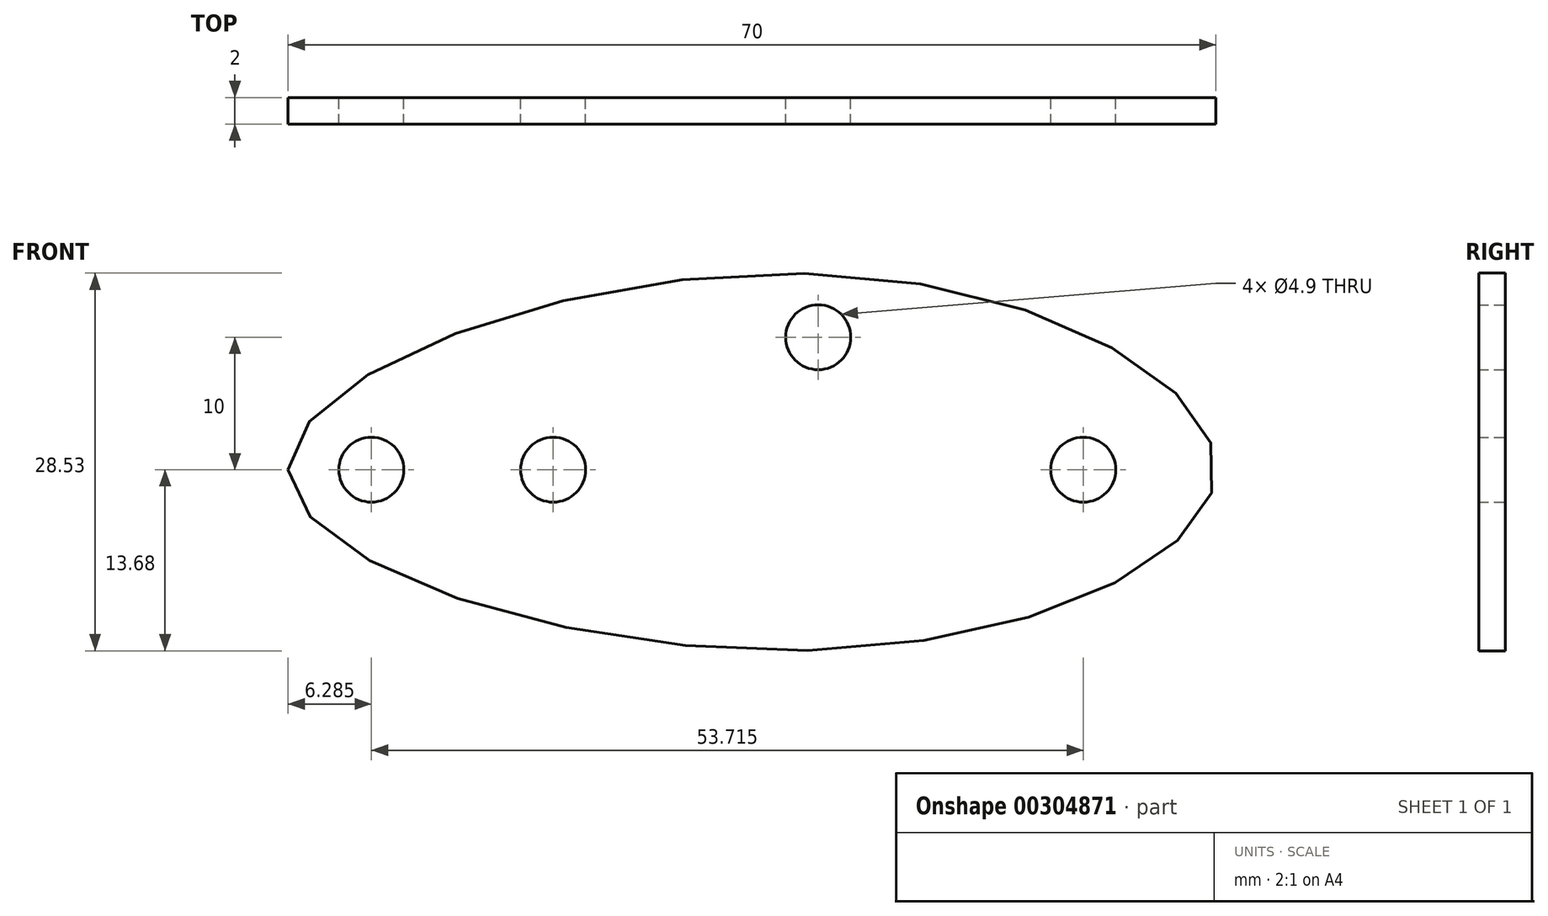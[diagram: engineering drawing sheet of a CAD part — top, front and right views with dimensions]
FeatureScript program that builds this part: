
annotation { "Feature Type Name" : "Feature", "Feature Type Description" : "" }
export const myFeature = defineFeature(function(context is Context, id is Id, definition is map)
    precondition{}
    {
        {
            var Q0;
            Q0=qCreatedBy(makeId("Front.planeOp"),FACE);
            var sketch = newSketch(context, id + "F0", { "sketchPlane" : qUnion([Q0])});
            skPoint(sketch, "E0", {"position": v(-20, 0) * mm});
            skPoint(sketch, "E1", {"position": v(20, 0) * mm});
            skCircle(sketch, "E2", {"center": v(-20, 0) * mm, "radius": 7.5 * mm});
            skCircle(sketch, "E3", {"center": v(20, 0) * mm, "radius": 7.5 * mm});
            skPoint(sketch, "E4", {"position": v(0, 0) * mm});
            skPoint(sketch, "E5", {"position": v(0, 10) * mm});
            skCircle(sketch, "E6", {"center": v(0, 10) * mm, "radius": 2.45 * mm});
            skCircle(sketch, "E7", {"center": v(-20, 0) * mm, "radius": 2.45 * mm});
            skCircle(sketch, "E8", {"center": v(20, 0) * mm, "radius": 2.45 * mm});
            skPoint(sketch, "E9", {"position": v(-33.71, 0) * mm});
            skCircle(sketch, "E10", {"center": v(-33.71, 0) * mm, "radius": 2.45 * mm});
            skSolve(sketch);
        }
        {
            var Q0;
            Q0=qCreatedBy(makeId("Front.planeOp"),FACE);
            var sketch = newSketch(context, id + "F1", { "sketchPlane" : qUnion([Q0])});
            skPoint(sketch, "E11", {"position": v(-40, 0) * mm});
            skPoint(sketch, "E12", {"position": v(30, 0) * mm});
            skFitSpline(sketch, "E13", {"points": [v(-40, 0) * mm, v(0, 14.81) * mm, v(30, 0) * mm, v(0, -13.65) * mm, v(-40, 0) * mm]});
            skSolve(sketch);
        }
        {
            var Q0;
            Q0=makeQuery(id+"F1.imprint","IMPRINT",FACE,{"disambiguationData":[TD([[makeQuery(id+"F1.imprint","IMPRINT",EDGE,{"derivedFrom":sQuery(id+"F1.wireOp",EDGE,"E13")}),-1.0]])]});
            extrude(context, id + "F2", {"entities" : qUnion([Q0]), "depth" : 2 * mm});
        }
        {
            var Q0;
            Q0=makeQuery(id+"F0.imprint","IMPRINT",FACE,{"disambiguationData":[TD([[makeQuery(id+"F0.imprint","IMPRINT",EDGE,{"derivedFrom":sQuery(id+"F0.wireOp",EDGE,"E7")}),1.0]])]});
            var Q1;
            Q1=makeQuery(id+"F0.imprint","IMPRINT",FACE,{"disambiguationData":[TD([[makeQuery(id+"F0.imprint","IMPRINT",EDGE,{"derivedFrom":sQuery(id+"F0.wireOp",EDGE,"E6")}),1.0]])]});
            var Q2;
            Q2=makeQuery(id+"F0.imprint","IMPRINT",FACE,{"disambiguationData":[TD([[makeQuery(id+"F0.imprint","IMPRINT",EDGE,{"derivedFrom":sQuery(id+"F0.wireOp",EDGE,"E8")}),1.0]])]});
            var Q3;
            Q3=makeQuery(id+"F0.imprint","IMPRINT",FACE,{"disambiguationData":[TD([[makeQuery(id+"F0.imprint","IMPRINT",EDGE,{"derivedFrom":sQuery(id+"F0.wireOp",EDGE,"E10")}),1.0]])]});
            extrude(context, id + "F3", {"entities" : qUnion([Q0, Q1, Q2, Q3]), "operationType" : NewBodyOperationType.REMOVE, "depth" : 25 * mm});
        }
    });
